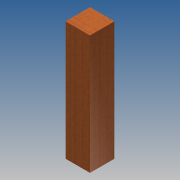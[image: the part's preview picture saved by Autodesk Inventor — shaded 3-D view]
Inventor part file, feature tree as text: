
AUTODESK INVENTOR PART (.ipt)
format: ipt  version: 2013 (Build 170138000, 138)  size: 79,872 bytes
history: native  units: in
note: dims shown in document units (in); Inventor stores cm internally (conversion verified against a paired STEP export)
features: extrude x1, sketch x1
ambient origin geometry x8: Origin, YZ Plane, XZ Plane, XY Plane, X Axis, Y Axis, Z Axis, Center Point
bodies: Solid1 (feature_tree)
feature tree (2):
  extrude  "Extrusion1"  Depth=3.5in
  sketch  "Sketch1"  dims[d0=3.5in d1=3.5in d2=17.0in d3=0.0in]
